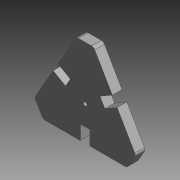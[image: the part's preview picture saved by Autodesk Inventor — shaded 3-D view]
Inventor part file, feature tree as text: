
AUTODESK INVENTOR PART (.ipt)
format: ipt  version: 2014 SP1 (Build 180222100, 222)  size: 117,760 bytes
history: native  units: in
note: dims shown in document units (in); Inventor stores cm internally (conversion verified against a paired STEP export)
features: extrude x2, sketch x2, pattern_circular x1, chamfer x1, fillet x1
ambient origin geometry x8: Origin, YZ Plane, XZ Plane, XY Plane, X Axis, Y Axis, Z Axis, Center Point
bodies: Solid1 (feature_tree)
feature tree (7):
  extrude  "Extrusion1"  Depth=0.0787in
  extrude  "Extrusion2"  Depth=0.3283in TaperAngle=0.0deg
  pattern_circular  "Circular Pattern1"  Count=3 Angle=360.0deg
  chamfer  "Chamfer1"  Distance=0.3937in Angle=45.0deg
  fillet  "Fillet1"  Radius=0.0787in
  sketch  "Sketch1"  dims[d0=0.0787in d1=0.7874in]
  sketch  "Sketch2"  dims[d2=0.2228in d3=0.0in d6=0.3396in d7=0.0in d8=1.1811in d9=360.0deg d11=0.3937in d12=0.0787in d13=45.0deg d14=0.0787in d15=0.3283in d16=0.1114in d17=0.1114in]
